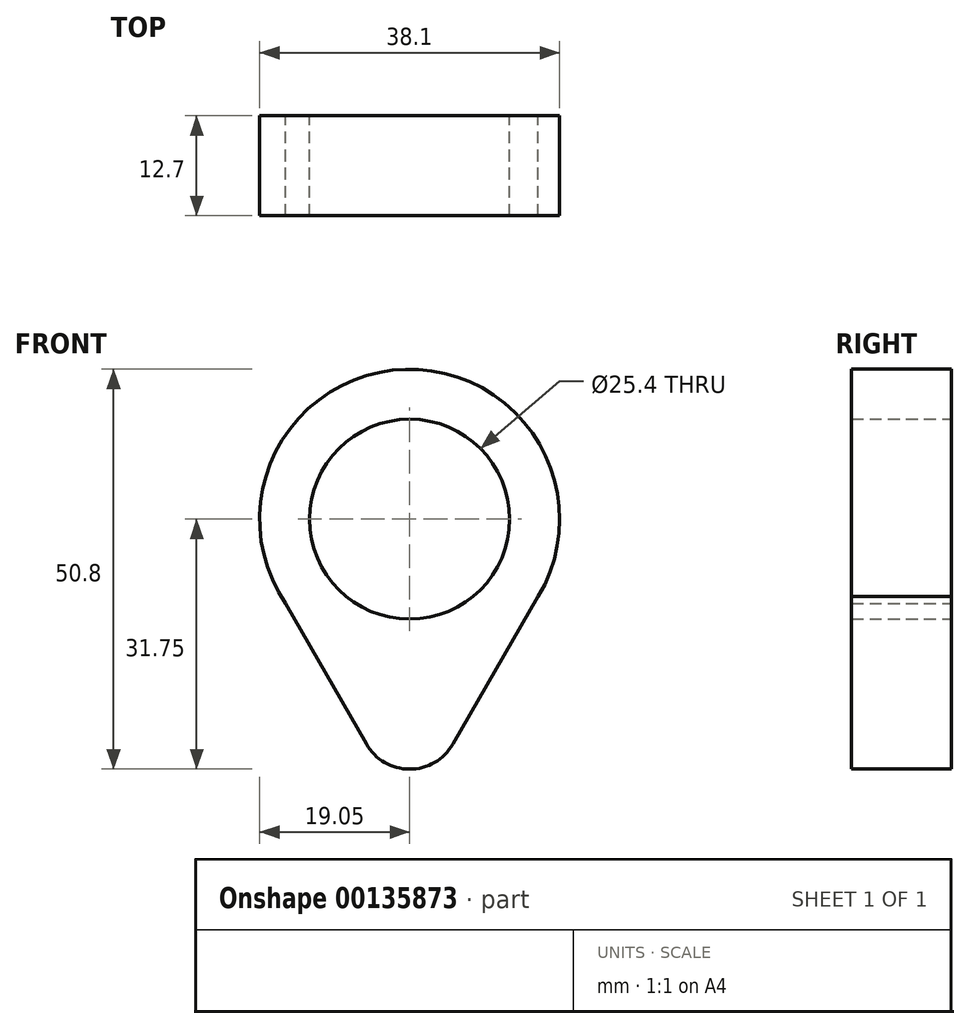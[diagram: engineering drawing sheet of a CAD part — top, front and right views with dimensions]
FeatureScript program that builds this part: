
annotation { "Feature Type Name" : "Feature", "Feature Type Description" : "" }
export const myFeature = defineFeature(function(context is Context, id is Id, definition is map)
    precondition{}
    {
        {
            var Q0;
            Q0=qCreatedBy(makeId("Front.planeOp"),FACE);
            var sketch = newSketch(context, id + "F0", { "sketchPlane" : qUnion([Q0])});
            skArc(sketch, "E0", {"start": v(16.33, -9.82) * mm, "mid": v(-0.54, 19.04) * mm, "end": v(-15.74, -10.73) * mm});
            skCircle(sketch, "E1", {"center": v(0, 0) * mm, "radius": 12.7 * mm});
            skArc(sketch, "E2", {"start": v(-5.5, -28.56) * mm, "mid": v(0, -31.75) * mm, "end": v(5.5, -28.57) * mm});
            skLineSegment(sketch, "E3", {"start": v(-15.74, -10.73) * mm, "end": v(-5.5, -28.56) * mm});
            skLineSegment(sketch, "E4", {"start": v(16.33, -9.82) * mm, "end": v(5.5, -28.57) * mm});
            skSolve(sketch);
        }
        {
            var Q0;
            Q0=makeQuery(id+"F0.imprint","IMPRINT",FACE,{"disambiguationData":[TD([[makeQuery(id+"F0.imprint","IMPRINT",EDGE,{"derivedFrom":sQuery(id+"F0.wireOp",EDGE,"E0")}),1.0]])]});
            extrude(context, id + "F1", {"entities" : qUnion([Q0]), "depth" : 12.7 * mm});
        }
    });
